# Revit family: MI-GARD
name_source: partatom
category: Plumbing Fixtures
revit_build: Autodesk Revit 2015 (Build: 20140322_1515(x64)
units: mm (PartAtom-declared; Revit-internal decimal feet)

## types (6) — shared parameters
A = 2"
ABS Frame = PC/ABS Plastic
Gasket Flexes = Rubber, Silicone
Manufacturer = MIFAB
Sealing Flapper = Rubber, Silicone
URL = www.mifab.com
V1 = Yes

## per-type parameters (varying)
| type | B | C | D | Description | EE | V2 | V3 |
| MI-GARD-15 | 1 45/128" | 1 85/128" | 41/64" | 1 1/2" Floor Drain Trap Seal | 87/128" | No | No |
| MI-GARD-2 | 1 45/64" | 2 13/64" | 103/128" | 2" Floor Drain Trap Seal | 109/128" | No | No |
| MI-GARD-3 | 2 5/8" | 3 13/64" | 1 15/64" | 3" Floor Drain Trap Seal | 1 5/16" | No | No |
| MI-GARD-35 | 3 9/32" | 3 103/128" | 1 35/64" | 3 1/2" Floor Drain Trap Seal | 1 41/64" | No | Yes |
| MI-GARD-4 | 3 87/128" | 4 13/64" | 1 47/64" | 4" Floor Drain Trap Seal | 1 27/32" | No | Yes |
| MI-GARD-6 | 5 87/128" | 6 13/64" | 2 87/128" | 6" Floor Drain Trap Seal | 2 27/32" | Yes | No |

note: column(s) folded — value = type name in every type: Model

## geometry (parser evidence)
native form markers: Sweep x2
no freeform markers — native parametric forms only
